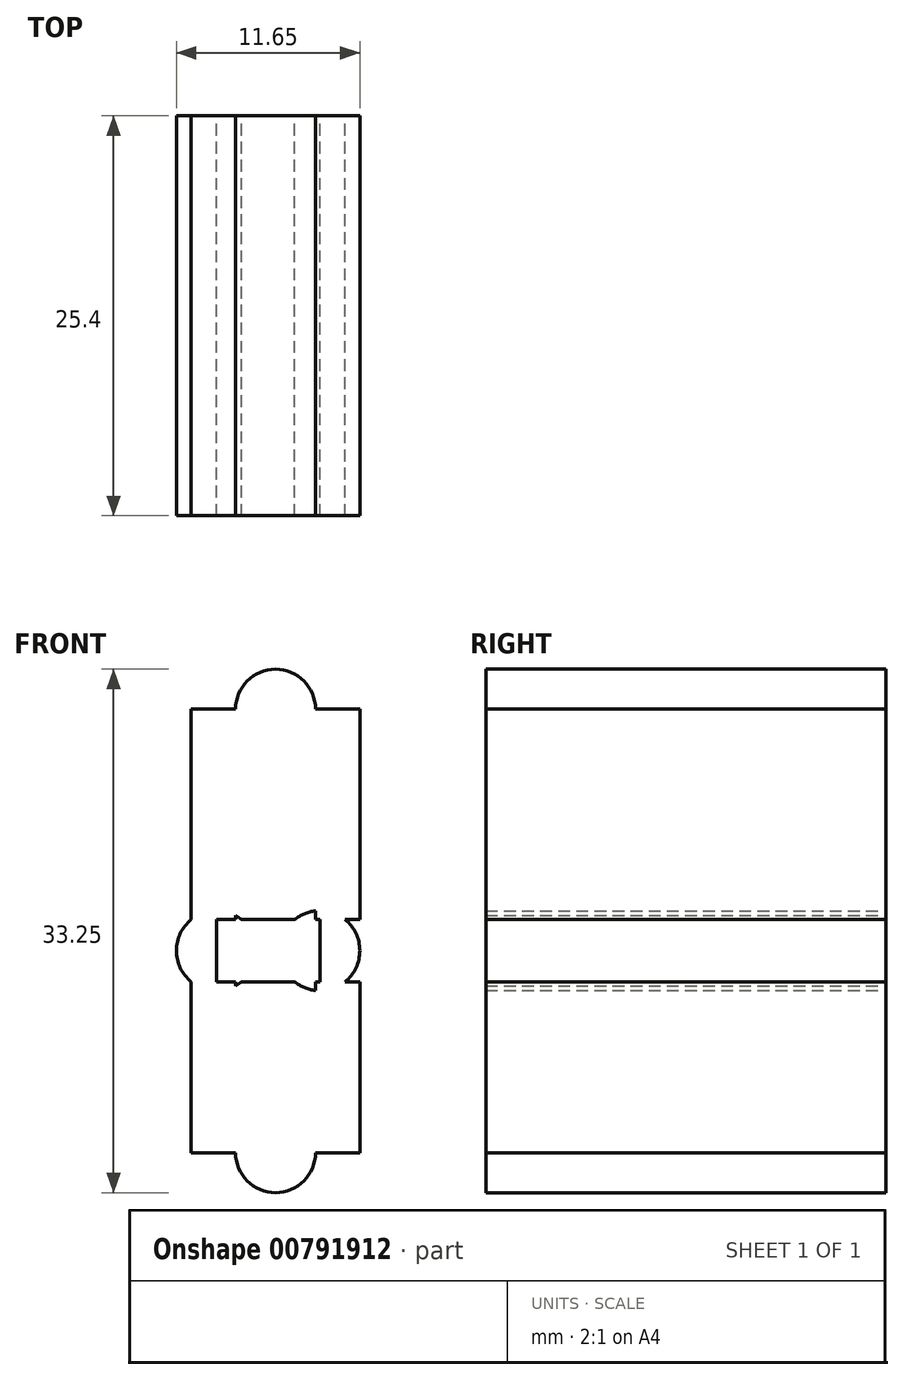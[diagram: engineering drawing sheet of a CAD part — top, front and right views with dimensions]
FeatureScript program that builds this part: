
annotation { "Feature Type Name" : "Feature", "Feature Type Description" : "" }
export const myFeature = defineFeature(function(context is Context, id is Id, definition is map)
    precondition{}
    {
        {
            var Q0;
            Q0=qCreatedBy(makeId("Front.planeOp"),FACE);
            var sketch = newSketch(context, id + "F0", { "sketchPlane" : qUnion([Q0])});
            skLineSegment(sketch, "E0.bottom", {"start": v(-19.06, -10.86) * mm, "end": v(-8.35, -10.86) * mm});
            skLineSegment(sketch, "E0.top", {"start": v(-19.06, 0) * mm, "end": v(-8.35, 0) * mm});
            skLineSegment(sketch, "E0.left", {"start": v(-19.06, -10.86) * mm, "end": v(-19.06, 0) * mm});
            skLineSegment(sketch, "E0.right", {"start": v(-8.35, -10.86) * mm, "end": v(-8.35, 0) * mm});
            skLineSegment(sketch, "E1.bottom", {"start": v(-19.06, 3.94) * mm, "end": v(-8.35, 3.94) * mm});
            skLineSegment(sketch, "E1.top", {"start": v(-19.06, 17.3) * mm, "end": v(-8.35, 17.3) * mm});
            skLineSegment(sketch, "E1.left", {"start": v(-19.06, 3.94) * mm, "end": v(-19.06, 17.3) * mm});
            skLineSegment(sketch, "E1.right", {"start": v(-8.35, 3.94) * mm, "end": v(-8.35, 17.3) * mm});
            skLineSegment(sketch, "E2", {"start": v(-17.46, 3.94) * mm, "end": v(-17.46, 0) * mm});
            skLineSegment(sketch, "E3", {"start": v(-10.9, 3.94) * mm, "end": v(-10.9, 0) * mm});
            skCircle(sketch, "E4", {"center": v(-10.9, 1.97) * mm, "radius": 2.54 * mm});
            skCircle(sketch, "E5", {"center": v(-17.46, 1.97) * mm, "radius": 2.54 * mm});
            skCircle(sketch, "E6", {"center": v(-13.7, 17.3) * mm, "radius": 2.54 * mm});
            skCircle(sketch, "E7", {"center": v(-13.7, -10.86) * mm, "radius": 2.54 * mm});
            skLineSegment(sketch, "E8", {"start": v(-16.25, -10.86) * mm, "end": v(-16.25, 17.3) * mm});
            skLineSegment(sketch, "E9", {"start": v(-11.17, -10.86) * mm, "end": v(-11.17, 17.3) * mm});
            skLineSegment(sketch, "E10", {"start": v(-15.86, 3.94) * mm, "end": v(-12.5, 3.94) * mm});
            skLineSegment(sketch, "E11", {"start": v(-15.86, 0) * mm, "end": v(-12.5, 0) * mm});
            skSolve(sketch);
        }
        {
            var Q0;
            Q0 = qSketchRegion(id + "F0", true);
            extrude(context, id + "F1", {"entities" : qUnion([Q0]), "depth" : 25.4 * mm, "offsetDistance" : 25.4 * mm});
        }
    });
